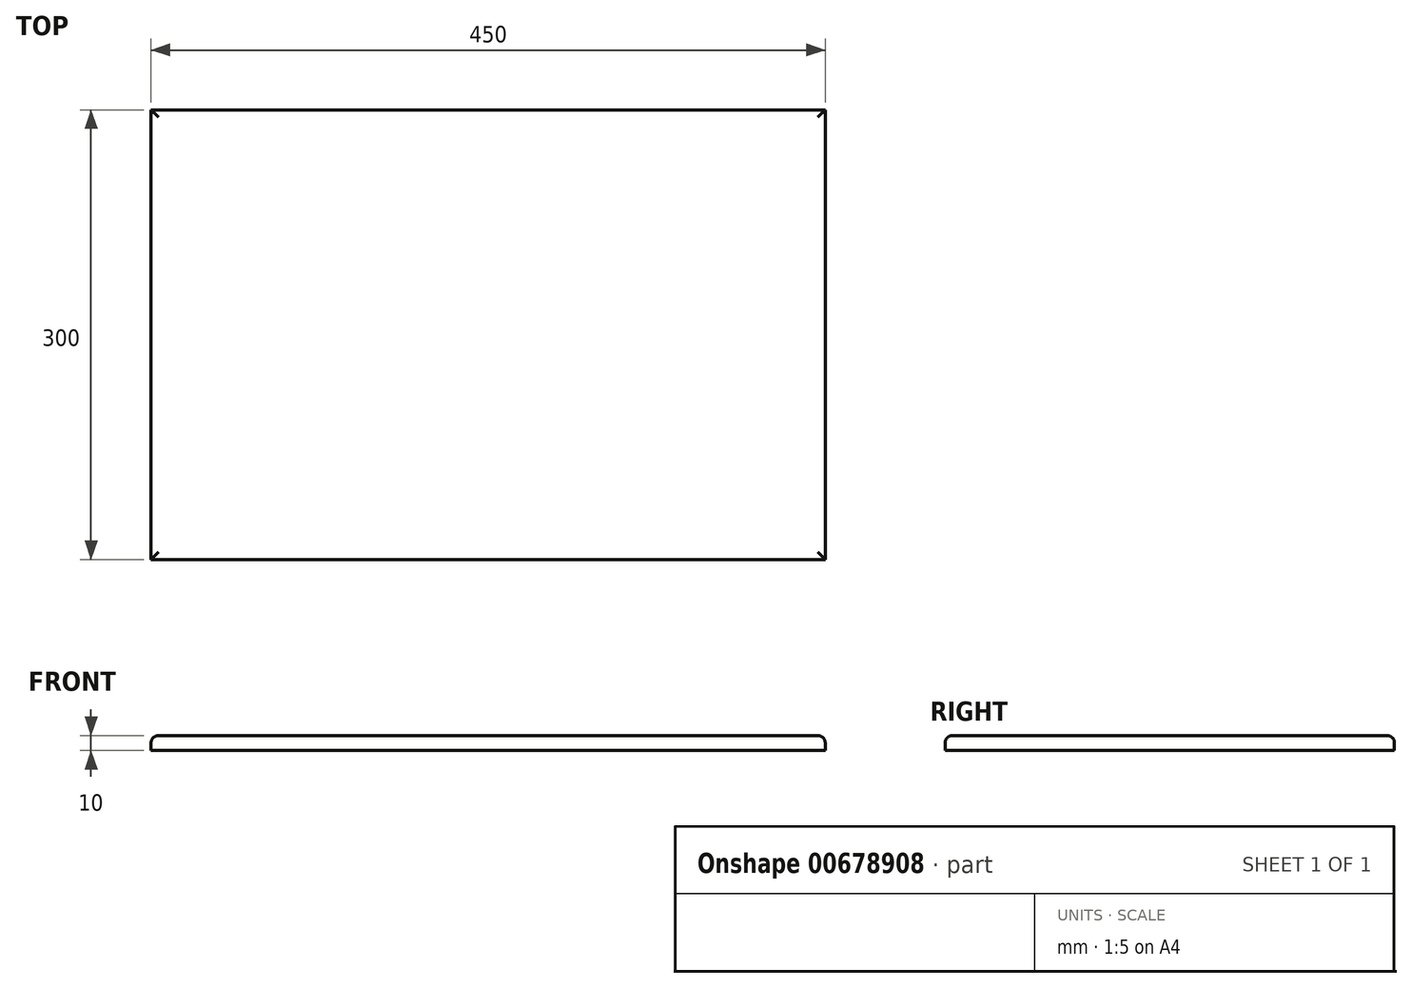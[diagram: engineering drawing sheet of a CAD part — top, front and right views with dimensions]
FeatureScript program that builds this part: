
annotation { "Feature Type Name" : "Feature", "Feature Type Description" : "" }
export const myFeature = defineFeature(function(context is Context, id is Id, definition is map)
    precondition{}
    {
        {
            var Q0;
            Q0=qCreatedBy(makeId("Top.planeOp"),FACE);
            var sketch = newSketch(context, id + "F0", { "sketchPlane" : qUnion([Q0])});
            skLineSegment(sketch, "E0.bottom", {"start": v(0, 0) * mm, "end": v(450, 0) * mm});
            skLineSegment(sketch, "E0.top", {"start": v(0, 300) * mm, "end": v(450, 300) * mm});
            skLineSegment(sketch, "E0.left", {"start": v(0, 0) * mm, "end": v(0, 300) * mm});
            skLineSegment(sketch, "E0.right", {"start": v(450, 0) * mm, "end": v(450, 300) * mm});
            skSolve(sketch);
        }
        {
            var Q0;
            Q0 = qSketchRegion(id + "F0", true);
            extrude(context, id + "F1", {"entities" : qUnion([Q0]), "depth" : 10 * mm, "offsetDistance" : 25 * mm});
        }
        {
            var Q0;
            Q0=makeQuery(id+"F1.opExtrude","CAP_FACE",FACE,{"disambiguationData":[OSD([sQuery(id+"F0.wireOp",EDGE,"E0.bottom"),sQuery(id+"F0.wireOp",EDGE,"E0.top"),sQuery(id+"F0.wireOp",EDGE,"E0.left"),sQuery(id+"F0.wireOp",EDGE,"E0.right")])],"isStart":false});
            fillet(context, id + "F2", {"entities" : qUnion([Q0]), "radius" : 5 * mm, "tangentPropagation" : true, "allowEdgeOverflow" : false});
        }
    });
